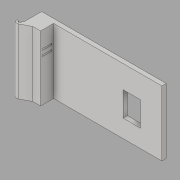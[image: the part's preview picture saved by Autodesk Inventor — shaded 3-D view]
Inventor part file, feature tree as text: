
AUTODESK INVENTOR PART (.ipt)
format: ipt  version: 2017 (Build 210142000, 142)  size: 124,416 bytes
history: native  units: in
note: dims shown in document units (in); Inventor stores cm internally (conversion verified against a paired STEP export)
features: extrude x3, sketch x3, projected_geometry x1
ambient origin geometry x8: Origin, YZ Plane, XZ Plane, XY Plane, X Axis, Y Axis, Z Axis, Center Point
bodies: Solid1 (feature_tree)
feature tree (7):
  extrude  "Extrusion1"  Depth=0.6in
  extrude  "Extrusion2"  Depth=0.0625in
  extrude  "Extrusion3"  Depth=0.45in
  sketch  "Sketch1"  dims[d0=3.0in d1=0.6in]
  sketch  "Sketch2"  dims[d2=0.1875in d3=0.0625in]
  projected_geometry  "Projected Loop1"
  sketch  "Sketch3"  dims[d4=0.75in d5=0.45in d6=0.75in d7=0.0in d8=5.0in d9=0.2in d10=0.0in d11=0.125in d12=0.08in d14=135.0deg d15=0.4in d16=3.0in d17=0.0in]
